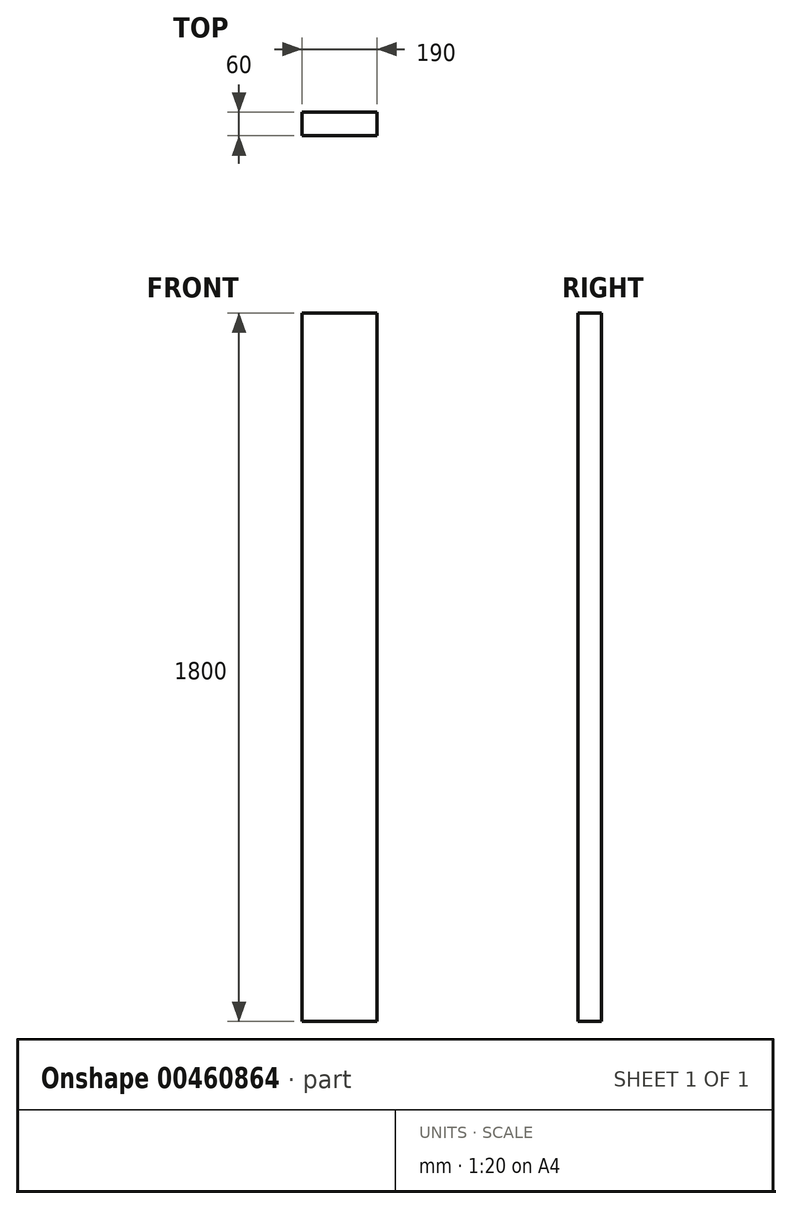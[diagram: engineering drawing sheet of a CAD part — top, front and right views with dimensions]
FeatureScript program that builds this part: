
annotation { "Feature Type Name" : "Feature", "Feature Type Description" : "" }
export const myFeature = defineFeature(function(context is Context, id is Id, definition is map)
    precondition{}
    {
        {
            var Q0;
            Q0=qCreatedBy(makeId("Front.planeOp"),FACE);
            var sketch = newSketch(context, id + "F0", { "sketchPlane" : qUnion([Q0])});
            skLineSegment(sketch, "E0.bottom", {"start": v(190, -3424.72) * mm, "end": v(0, -3424.72) * mm});
            skLineSegment(sketch, "E0.top", {"start": v(190, -5224.72) * mm, "end": v(0, -5224.72) * mm});
            skLineSegment(sketch, "E0.left", {"start": v(190, -3424.72) * mm, "end": v(190, -5224.72) * mm});
            skLineSegment(sketch, "E0.right", {"start": v(0, -3424.72) * mm, "end": v(0, -5224.72) * mm});
            skSolve(sketch);
        }
        {
            var Q0;
            Q0=makeQuery(id+"F0.imprint","IMPRINT",FACE,{"disambiguationData":[TD([[makeQuery(id+"F0.imprint","IMPRINT",EDGE,{"derivedFrom":sQuery(id+"F0.wireOp",EDGE,"E0.bottom")}),1.0]])]});
            extrude(context, id + "F1", {"entities" : qUnion([Q0]), "depth" : 60 * mm});
        }
    });
